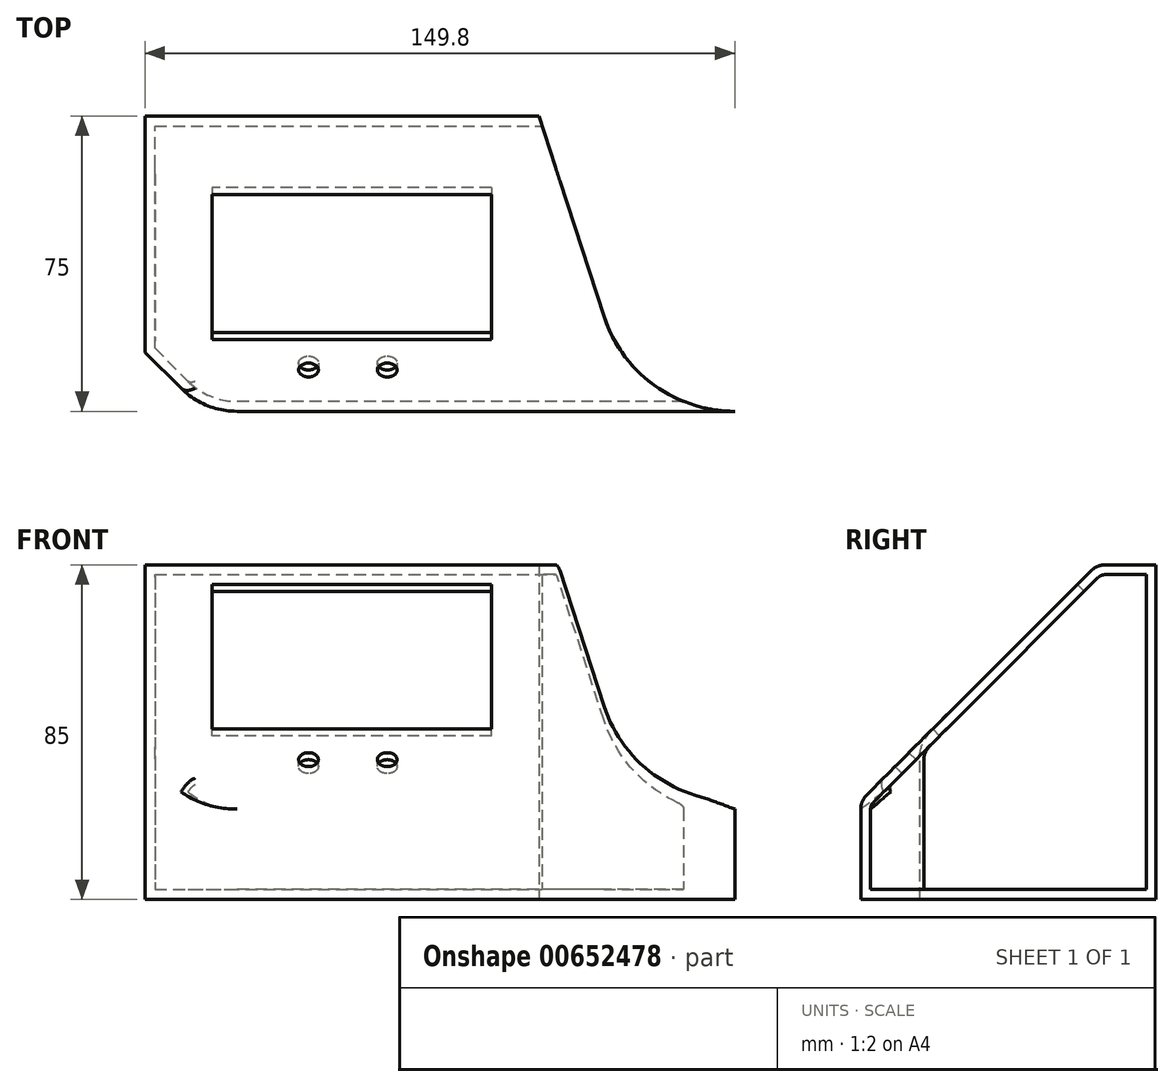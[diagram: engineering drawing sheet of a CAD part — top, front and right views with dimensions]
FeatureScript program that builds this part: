
annotation { "Feature Type Name" : "Feature", "Feature Type Description" : "" }
export const myFeature = defineFeature(function(context is Context, id is Id, definition is map)
    precondition{}
    {
        {
            var Q0;
            Q0=qCreatedBy(makeId("Top.planeOp"),FACE);
            var sketch = newSketch(context, id + "F0", { "sketchPlane" : qUnion([Q0])});
            skCircle(sketch, "E0.cCircle", {"center": v(0, 0) * mm, "radius": 85 * mm, "construction": true});
            skLineSegment(sketch, "E0.0", {"start": v(92.07, 8.28) * mm, "end": v(69.61, -60.82) * mm});
            skLineSegment(sketch, "E0.1", {"start": v(36.33, -85) * mm, "end": v(-36.33, -85) * mm});
            skLineSegment(sketch, "E0.2", {"start": v(-69.61, -60.82) * mm, "end": v(-92.07, 8.28) * mm});
            skLineSegment(sketch, "E0.3", {"start": v(-79.35, 47.41) * mm, "end": v(-20.57, 90.12) * mm});
            skLineSegment(sketch, "E0.4", {"start": v(20.57, 90.12) * mm, "end": v(79.35, 47.41) * mm});
            skPoint(sketch, "E0.0.midPoint", {"position": v(80.84, -26.27) * mm});
            skPoint(sketch, "E1.visualSharp", {"position": v(-99.92, 32.47) * mm});
            skArc(sketch, "E1.filletArc", {"start": v(-79.35, 47.41) * mm, "mid": v(-92.07, 29.91) * mm, "end": v(-92.07, 8.28) * mm});
            skPoint(sketch, "E2.visualSharp", {"position": v(-61.76, -85) * mm});
            skArc(sketch, "E2.filletArc", {"start": v(-69.61, -60.82) * mm, "mid": v(-56.9, -78.32) * mm, "end": v(-36.33, -85) * mm});
            skPoint(sketch, "E3.visualSharp", {"position": v(61.76, -85) * mm});
            skArc(sketch, "E3.filletArc", {"start": v(36.33, -85) * mm, "mid": v(56.9, -78.32) * mm, "end": v(69.61, -60.82) * mm});
            skPoint(sketch, "E4.visualSharp", {"position": v(99.92, 32.47) * mm});
            skArc(sketch, "E4.filletArc", {"start": v(92.07, 8.28) * mm, "mid": v(92.07, 29.91) * mm, "end": v(79.35, 47.41) * mm});
            skPoint(sketch, "E5.visualSharp", {"position": v(0, 105.07) * mm});
            skArc(sketch, "E5.filletArc", {"start": v(20.57, 90.12) * mm, "mid": v(0, 96.8) * mm, "end": v(-20.57, 90.12) * mm});
            skArc(sketch, "E6.0", {"start": v(89.21, 9.2) * mm, "mid": v(89.21, 28.99) * mm, "end": v(77.59, 44.99) * mm});
            skLineSegment(sketch, "E6.1", {"start": v(18.8, 87.7) * mm, "end": v(77.59, 44.99) * mm});
            skLineSegment(sketch, "E6.2", {"start": v(89.21, 9.2) * mm, "end": v(66.76, -59.89) * mm});
            skArc(sketch, "E6.3", {"start": v(18.8, 87.7) * mm, "mid": v(0, 93.8) * mm, "end": v(-18.8, 87.7) * mm});
            skLineSegment(sketch, "E6.4", {"start": v(-77.59, 44.99) * mm, "end": v(-18.8, 87.7) * mm});
            skArc(sketch, "E6.5", {"start": v(-77.59, 44.99) * mm, "mid": v(-89.21, 28.99) * mm, "end": v(-89.21, 9.2) * mm});
            skArc(sketch, "E6.6", {"start": v(36.33, -82) * mm, "mid": v(55.14, -75.89) * mm, "end": v(66.76, -59.89) * mm});
            skLineSegment(sketch, "E6.7", {"start": v(36.33, -82) * mm, "end": v(-36.33, -82) * mm});
            skArc(sketch, "E6.8", {"start": v(-66.76, -59.89) * mm, "mid": v(-55.14, -75.89) * mm, "end": v(-36.33, -82) * mm});
            skLineSegment(sketch, "E6.9", {"start": v(-66.76, -59.89) * mm, "end": v(-89.21, 9.2) * mm});
            skCircle(sketch, "E7", {"center": v(-90.26, 29.33) * mm, "radius": 0.9 * mm});
            skCircle(sketch, "E8", {"center": v(79.03, -25.68) * mm, "radius": 0.9 * mm});
            skPoint(sketch, "E9", {"position": v(-89.21, 28.99) * mm});
            skLineSegment(sketch, "E10.0", {"start": v(-89.21, 28.99) * mm, "end": v(-90.26, 29.33) * mm, "construction": true});
            skLineSegment(sketch, "E11.0", {"start": v(80.84, -26.27) * mm, "end": v(0, 0) * mm, "construction": true});
            skCircle(sketch, "E12", {"center": v(0, 0) * mm, "radius": 20 * mm});
            skLineSegment(sketch, "E13", {"start": v(-19.66, 3.7) * mm, "end": v(-36.33, -85) * mm});
            skLineSegment(sketch, "E14", {"start": v(19.66, 3.7) * mm, "end": v(36.33, -85) * mm});
            skLineSegment(sketch, "E15", {"start": v(-36.33, -85) * mm, "end": v(-186.13, -85) * mm});
            skLineSegment(sketch, "E16", {"start": v(-186.13, -85) * mm, "end": v(-186.13, -10) * mm});
            skLineSegment(sketch, "E17", {"start": v(-186.13, -10) * mm, "end": v(-86.13, -10) * mm});
            skLineSegment(sketch, "E18", {"start": v(-86.13, -10) * mm, "end": v(-78.23, -10) * mm});
            skSolve(sketch);
        }
        {
            var Q0;
            {var subQ0=sQuery(id+"F0.wireOp",EDGE,"E2.filletArc");Q0=makeQuery(id+"F0.imprint","IMPRINT",FACE,{"disambiguationData":[TD([[makeQuery(id+"F0.imprint","IMPRINT",EDGE,{"derivedFrom":subQ0}),-1.0]])]});}
            extrude(context, id + "F1", {"entities" : qUnion([Q0]), "depth" : 85 * mm, "offsetDistance" : 25 * mm});
        }
        {
            var Q0;
            Q0=makeQuery(id+"F1.opExtrude","CAP_EDGE",EDGE,{"disambiguationData":[OSD([sQuery(id+"F0.wireOp",EDGE,"E15")])],"isStart":false});
            chamfer(context, id + "F2", {"entities" : qUnion([Q0]), "chamferType" : ChamferType.OFFSET_ANGLE, "width" : 60 * mm, "oppositeDirection" : false, "angle" : 45 * degree, "tangentPropagation" : true});
        }
        {
            var Q0;
            Q0=makeQuery(id+"F2.opChamfer","BLEND_FACE",FACE,{"disambiguationData":[OSD([sQuery(id+"F0.wireOp",EDGE,"E15")])]});
            var sketch = newSketch(context, id + "F3", { "sketchPlane" : qUnion([Q0])});
            skLineSegment(sketch, "E19.bottom", {"start": v(-182.13, 37.43) * mm, "end": v(-87.13, 37.43) * mm});
            skLineSegment(sketch, "E19.top", {"start": v(-182.13, -17.57) * mm, "end": v(-87.13, -17.57) * mm});
            skLineSegment(sketch, "E19.left", {"start": v(-182.13, 37.43) * mm, "end": v(-182.13, -17.57) * mm});
            skLineSegment(sketch, "E19.right", {"start": v(-87.13, 37.43) * mm, "end": v(-87.13, -17.57) * mm});
            skLineSegment(sketch, "E20", {"start": v(-134.63, 37.43) * mm, "end": v(-134.63, -17.57) * mm, "construction": true});
            skCircle(sketch, "E21", {"center": v(-144.63, -27.57) * mm, "radius": 2.5 * mm});
            skCircle(sketch, "E22", {"center": v(-124.63, -27.57) * mm, "radius": 2.5 * mm});
            skLineSegment(sketch, "E23", {"start": v(-144.63, -27.57) * mm, "end": v(-124.63, -27.57) * mm, "construction": true});
            skPoint(sketch, "E24", {"position": v(-134.63, -27.57) * mm});
            skLineSegment(sketch, "E25.bottom", {"start": v(-169.13, 35.43) * mm, "end": v(-98.13, 35.43) * mm});
            skLineSegment(sketch, "E25.top", {"start": v(-169.13, -16.57) * mm, "end": v(-98.13, -16.57) * mm});
            skLineSegment(sketch, "E25.left", {"start": v(-169.13, 35.43) * mm, "end": v(-169.13, -16.57) * mm});
            skLineSegment(sketch, "E25.right", {"start": v(-98.13, 35.43) * mm, "end": v(-98.13, -16.57) * mm});
            skSolve(sketch);
        }
        {
            var Q0;
            Q0=makeQuery(id+"F1.opExtrude","SWEPT_EDGE",EDGE,{"disambiguationData":[OSD([sQuery(id+"F0.wireOp",EDGE,"E15"),sQuery(id+"F0.wireOp",EDGE,"E16")])]});
            chamfer(context, id + "F4", {"entities" : qUnion([Q0]), "width" : 15 * mm, "tangentPropagation" : true});
        }
        {
            var Q0;
            {var subQ0=sQuery(id+"F0.wireOp",EDGE,"E15");Q0=makeQuery(id+"F4.opChamfer","BLEND_EDGE",EDGE,{"blendedFrom":[makeQuery(id+"F1.opExtrude","SWEPT_EDGE",EDGE,{"disambiguationData":[OSD([subQ0,sQuery(id+"F0.wireOp",EDGE,"E16")])]}),makeQuery(id+"F1.opExtrude","SWEPT_FACE",FACE,{"disambiguationData":[OSD([subQ0])]})],"blendedInto":[makeQuery(id+"F1.opExtrude","SWEPT_FACE",FACE,{"disambiguationData":[OSD([subQ0])]})]});}
            fillet(context, id + "F5", {"entities" : qUnion([Q0]), "radius" : 20 * mm, "tangentPropagation" : true, "allowEdgeOverflow" : false});
        }
        {
            var Q0;
            {var subQ0=sQuery(id+"F0.wireOp",EDGE,"E15");Q0=makeQuery(id+"F2.opChamfer","BLEND_EDGE",EDGE,{"blendedFrom":[makeQuery(id+"F1.opExtrude","CAP_EDGE",EDGE,{"disambiguationData":[OSD([subQ0])],"isStart":false}),makeQuery(id+"F1.opExtrude","CAP_FACE",FACE,{"disambiguationData":[OSD([sQuery(id+"F0.wireOp",EDGE,"E0.2"),sQuery(id+"F0.wireOp",EDGE,"E2.filletArc"),subQ0,sQuery(id+"F0.wireOp",EDGE,"E16"),sQuery(id+"F0.wireOp",EDGE,"E17")])],"isStart":false})],"blendedInto":[makeQuery(id+"F1.opExtrude","CAP_FACE",FACE,{"disambiguationData":[OSD([sQuery(id+"F0.wireOp",EDGE,"E0.2"),sQuery(id+"F0.wireOp",EDGE,"E2.filletArc"),subQ0,sQuery(id+"F0.wireOp",EDGE,"E16"),sQuery(id+"F0.wireOp",EDGE,"E17")])],"isStart":false})]});}
            var Q1;
            {var subQ0=sQuery(id+"F0.wireOp",EDGE,"E15");Q1=makeQuery(id+"F2.opChamfer","BLEND_EDGE",EDGE,{"blendedFrom":[makeQuery(id+"F1.opExtrude","CAP_EDGE",EDGE,{"disambiguationData":[OSD([subQ0])],"isStart":false}),makeQuery(id+"F1.opExtrude","SWEPT_FACE",FACE,{"disambiguationData":[OSD([subQ0])]})],"blendedInto":[makeQuery(id+"F1.opExtrude","SWEPT_FACE",FACE,{"disambiguationData":[OSD([subQ0])]})]});}
            fillet(context, id + "F6", {"entities" : qUnion([Q0, Q1]), "radius" : 5 * mm, "tangentPropagation" : true, "allowEdgeOverflow" : false});
        }
        {
            var Q0;
            Q0=makeQuery(id+"F1.opExtrude","SWEPT_FACE",FACE,{"disambiguationData":[OSD([sQuery(id+"F0.wireOp",EDGE,"E2.filletArc")])]});
            var Q1;
            Q1=makeQuery(id+"F1.opExtrude","SWEPT_FACE",FACE,{"disambiguationData":[OSD([sQuery(id+"F0.wireOp",EDGE,"E0.2")])]});
            shell(context, id + "F7", {"entities" : qUnion([Q0, Q1]), "thickness" : 2.5 * mm});
        }
        {
            var Q0;
            Q0=makeQuery(id+"F3.imprint","IMPRINT",FACE,{"disambiguationData":[TD([[makeQuery(id+"F3.imprint","IMPRINT",EDGE,{"derivedFrom":sQuery(id+"F3.wireOp",EDGE,"E25.bottom")}),-1.0]])]});
            var Q1;
            Q1=makeQuery(id+"F3.imprint","IMPRINT",FACE,{"disambiguationData":[TD([[makeQuery(id+"F3.imprint","IMPRINT",EDGE,{"derivedFrom":sQuery(id+"F3.wireOp",EDGE,"E21")}),1.0]])]});
            var Q2;
            Q2=makeQuery(id+"F3.imprint","IMPRINT",FACE,{"disambiguationData":[TD([[makeQuery(id+"F3.imprint","IMPRINT",EDGE,{"derivedFrom":sQuery(id+"F3.wireOp",EDGE,"E22")}),1.0]])]});
            extrude(context, id + "F8", {"entities" : qUnion([Q0, Q1, Q2]), "operationType" : NewBodyOperationType.REMOVE, "oppositeDirection" : true, "depth" : 10 * mm, "offsetDistance" : 25 * mm});
        }
    });
